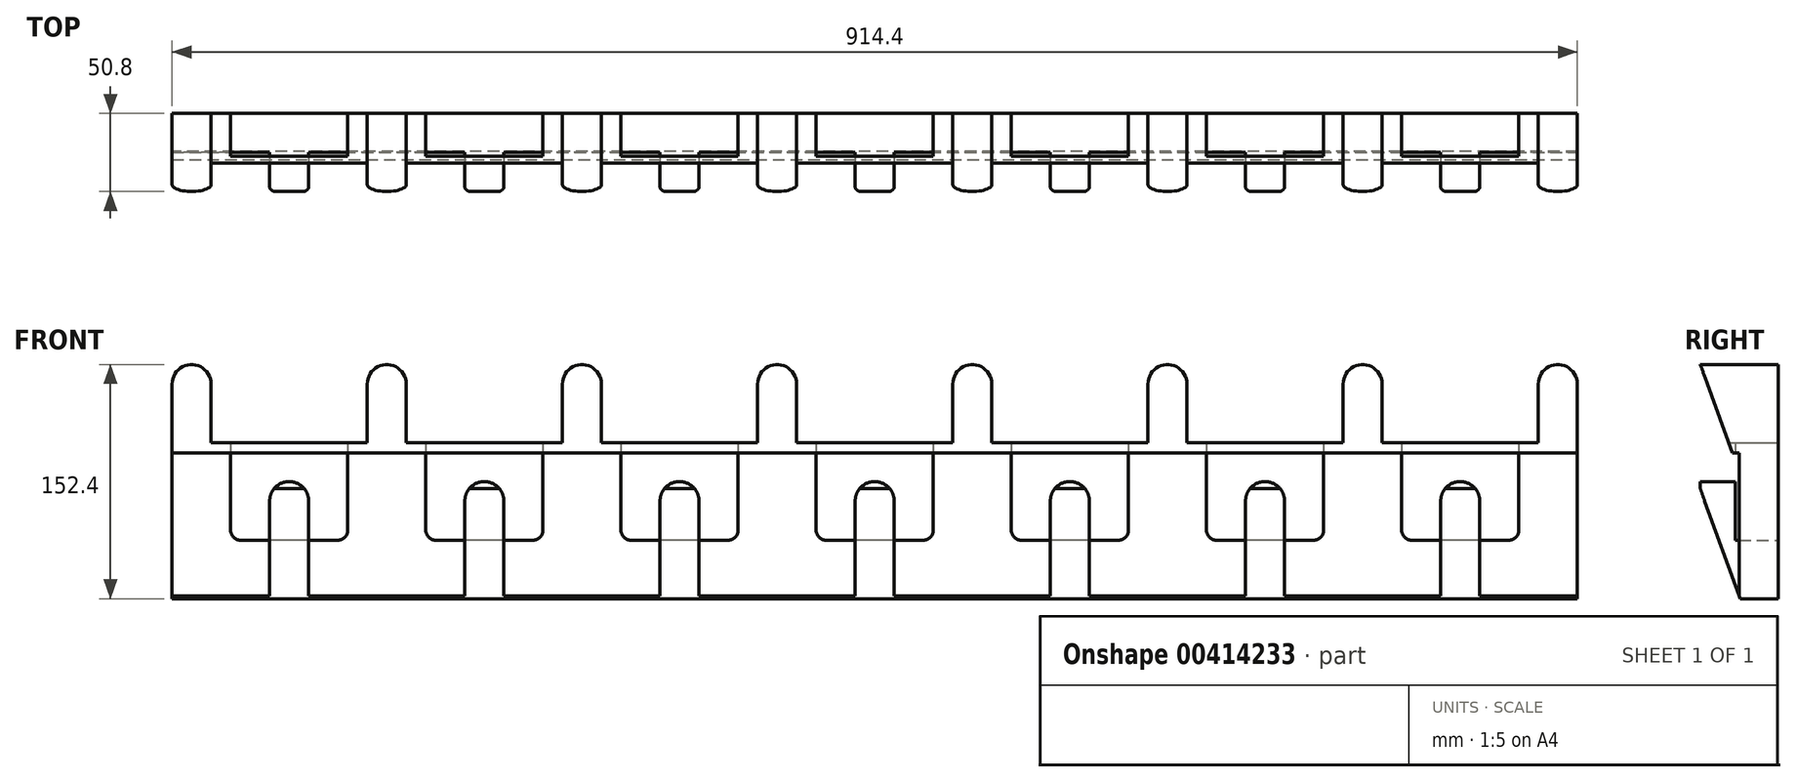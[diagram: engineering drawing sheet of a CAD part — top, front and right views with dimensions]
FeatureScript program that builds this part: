
annotation { "Feature Type Name" : "Feature", "Feature Type Description" : "" }
export const myFeature = defineFeature(function(context is Context, id is Id, definition is map)
    precondition{}
    {
        {
            var Q0;
            Q0=qCreatedBy(makeId("Right.planeOp"),FACE);
            var sketch = newSketch(context, id + "F0", { "sketchPlane" : qUnion([Q0])});
            skLineSegment(sketch, "E0.bottom", {"start": v(-50.8, 125.41) * mm, "end": v(0, 125.41) * mm});
            skLineSegment(sketch, "E0.top", {"start": v(-50.8, -26.99) * mm, "end": v(0, -26.99) * mm});
            skLineSegment(sketch, "E0.left", {"start": v(-50.8, 125.41) * mm, "end": v(-50.8, -26.99) * mm});
            skLineSegment(sketch, "E0.right", {"start": v(0, 125.41) * mm, "end": v(0, -26.99) * mm});
            skSolve(sketch);
        }
        {
            var Q0;
            Q0 = qSketchRegion(id + "F0", true);
            extrude(context, id + "F1", {"entities" : qUnion([Q0]), "depth" : 914.4 * mm});
        }
        {
            var Q0;
            Q0=makeQuery(id+"F1.opExtrude","SWEPT_FACE",FACE,{"disambiguationData":[OSD([sQuery(id+"F0.wireOp",EDGE,"E0.left")])]});
            var sketch = newSketch(context, id + "F2", { "sketchPlane" : qUnion([Q0])});
            skLineSegment(sketch, "E1.left", {"start": v(63.5, -26.99) * mm, "end": v(63.5, 36.51) * mm});
            skArc(sketch, "E2", {"start": v(88.9, 36.51) * mm, "mid": v(76.2, 49.21) * mm, "end": v(63.5, 36.51) * mm});
            skLineSegment(sketch, "E3", {"start": v(63.5, -26.99) * mm, "end": v(-24.16, -26.99) * mm});
            skLineSegment(sketch, "E4", {"start": v(88.9, 36.51) * mm, "end": v(88.9, -26.99) * mm});
            skArc(sketch, "E5.1.0.0", {"start": v(215.9, 36.51) * mm, "mid": v(203.2, 49.21) * mm, "end": v(190.5, 36.51) * mm});
            skLineSegment(sketch, "E5.1.0.1", {"start": v(215.9, 36.51) * mm, "end": v(215.9, -26.99) * mm});
            skLineSegment(sketch, "E5.1.0.2", {"start": v(190.5, -26.99) * mm, "end": v(190.5, 36.51) * mm});
            skArc(sketch, "E5.2.0.0", {"start": v(342.9, 36.51) * mm, "mid": v(330.2, 49.21) * mm, "end": v(317.5, 36.51) * mm});
            skLineSegment(sketch, "E5.2.0.1", {"start": v(342.9, 36.51) * mm, "end": v(342.9, -26.99) * mm});
            skLineSegment(sketch, "E5.2.0.2", {"start": v(317.5, -26.99) * mm, "end": v(317.5, 36.51) * mm});
            skArc(sketch, "E5.3.0.0", {"start": v(469.9, 36.51) * mm, "mid": v(457.2, 49.21) * mm, "end": v(444.5, 36.51) * mm});
            skLineSegment(sketch, "E5.3.0.1", {"start": v(469.9, 36.51) * mm, "end": v(469.9, -26.99) * mm});
            skLineSegment(sketch, "E5.3.0.2", {"start": v(444.5, -26.99) * mm, "end": v(444.5, 36.51) * mm});
            skArc(sketch, "E5.4.0.0", {"start": v(596.9, 36.51) * mm, "mid": v(584.2, 49.21) * mm, "end": v(571.5, 36.51) * mm});
            skLineSegment(sketch, "E5.4.0.1", {"start": v(596.9, 36.51) * mm, "end": v(596.9, -26.99) * mm});
            skLineSegment(sketch, "E5.4.0.2", {"start": v(571.5, -26.99) * mm, "end": v(571.5, 36.51) * mm});
            skArc(sketch, "E5.5.0.0", {"start": v(723.9, 36.51) * mm, "mid": v(711.2, 49.21) * mm, "end": v(698.5, 36.51) * mm});
            skLineSegment(sketch, "E5.5.0.1", {"start": v(723.9, 36.51) * mm, "end": v(723.9, -26.99) * mm});
            skLineSegment(sketch, "E5.5.0.2", {"start": v(698.5, -26.99) * mm, "end": v(698.5, 36.51) * mm});
            skArc(sketch, "E5.6.0.0", {"start": v(850.9, 36.51) * mm, "mid": v(838.2, 49.21) * mm, "end": v(825.5, 36.51) * mm});
            skLineSegment(sketch, "E5.6.0.1", {"start": v(850.9, 36.51) * mm, "end": v(850.9, -26.99) * mm});
            skLineSegment(sketch, "E5.6.0.2", {"start": v(825.5, -26.99) * mm, "end": v(825.5, 36.51) * mm});
            skLineSegment(sketch, "E5.direction1", {"start": v(63.5, -26.99) * mm, "end": v(190.5, -26.99) * mm, "construction": true});
            skLineSegment(sketch, "E6", {"start": v(88.9, -26.99) * mm, "end": v(190.5, -26.99) * mm});
            skLineSegment(sketch, "E7", {"start": v(215.9, -26.99) * mm, "end": v(317.5, -26.99) * mm});
            skLineSegment(sketch, "E8", {"start": v(342.9, -26.99) * mm, "end": v(444.5, -26.99) * mm});
            skLineSegment(sketch, "E9", {"start": v(469.9, -26.99) * mm, "end": v(571.5, -26.99) * mm});
            skLineSegment(sketch, "E10", {"start": v(596.9, -26.99) * mm, "end": v(698.5, -26.99) * mm});
            skLineSegment(sketch, "E11", {"start": v(723.9, -26.99) * mm, "end": v(825.5, -26.99) * mm});
            skLineSegment(sketch, "E12", {"start": v(850.9, -26.99) * mm, "end": v(949.6, -26.99) * mm});
            skLineSegment(sketch, "E13", {"start": v(949.6, -26.99) * mm, "end": v(949.6, 67.97) * mm});
            skLineSegment(sketch, "E14", {"start": v(949.6, 67.97) * mm, "end": v(-24.16, 67.97) * mm});
            skLineSegment(sketch, "E15", {"start": v(-24.16, 67.97) * mm, "end": v(-24.16, -26.99) * mm});
            skSolve(sketch);
        }
        {
            var Q0;
            Q0 = qSketchRegion(id + "F2", true);
            extrude(context, id + "F3", {"entities" : qUnion([Q0]), "operationType" : NewBodyOperationType.REMOVE, "oppositeDirection" : true, "depth" : 25.4 * mm});
        }
        {
            var Q0;
            Q0=qCreatedBy(makeId("Right.planeOp"),FACE);
            var sketch = newSketch(context, id + "F4", { "sketchPlane" : qUnion([Q0])});
            skLineSegment(sketch, "E16", {"start": v(-24.74, -26.99) * mm, "end": v(-50.8, 44.62) * mm});
            skLineSegment(sketch, "E17", {"start": v(-50.8, 44.62) * mm, "end": v(-50.8, -26.99) * mm});
            skLineSegment(sketch, "E18", {"start": v(-50.8, -26.99) * mm, "end": v(-24.74, -26.99) * mm});
            skSolve(sketch);
        }
        {
            var Q0;
            Q0 = qSketchRegion(id + "F4", true);
            extrude(context, id + "F5", {"entities" : qUnion([Q0]), "operationType" : NewBodyOperationType.REMOVE, "endBound" : BoundingType.THROUGH_ALL, "depth" : 25.4 * mm});
        }
        {
            var Q0;
            Q0=qCreatedBy(makeId("Right.planeOp"),FACE);
            var sketch = newSketch(context, id + "F6", { "sketchPlane" : qUnion([Q0])});
            skLineSegment(sketch, "E19", {"start": v(-29.08, 65.74) * mm, "end": v(-50.8, 125.41) * mm});
            skLineSegment(sketch, "E20", {"start": v(-50.8, 125.41) * mm, "end": v(-50.8, 65.74) * mm});
            skLineSegment(sketch, "E21", {"start": v(-50.8, 65.74) * mm, "end": v(-29.08, 65.74) * mm});
            skSolve(sketch);
        }
        {
            var Q0;
            Q0 = qSketchRegion(id + "F6", true);
            extrude(context, id + "F7", {"entities" : qUnion([Q0]), "operationType" : NewBodyOperationType.REMOVE, "endBound" : BoundingType.THROUGH_ALL, "depth" : 25.4 * mm});
        }
        {
            var Q0;
            Q0=qCreatedBy(makeId("Front.planeOp"),FACE);
            var sketch = newSketch(context, id + "F8", { "sketchPlane" : qUnion([Q0])});
            skLineSegment(sketch, "E22", {"start": v(0, 74.61) * mm, "end": v(0, 112.71) * mm});
            skLineSegment(sketch, "E23", {"start": v(25.4, 112.71) * mm, "end": v(25.4, 74.61) * mm});
            skArc(sketch, "E24", {"start": v(25.4, 112.71) * mm, "mid": v(12.7, 125.41) * mm, "end": v(0, 112.71) * mm});
            skLineSegment(sketch, "E25.1.0.0", {"start": v(152.4, 112.71) * mm, "end": v(152.4, 74.61) * mm});
            skArc(sketch, "E25.1.0.1", {"start": v(152.4, 112.71) * mm, "mid": v(139.7, 125.41) * mm, "end": v(127, 112.71) * mm});
            skLineSegment(sketch, "E25.1.0.2", {"start": v(127, 74.61) * mm, "end": v(127, 112.71) * mm});
            skLineSegment(sketch, "E25.2.0.0", {"start": v(279.4, 112.71) * mm, "end": v(279.4, 74.61) * mm});
            skArc(sketch, "E25.2.0.1", {"start": v(279.4, 112.71) * mm, "mid": v(266.7, 125.41) * mm, "end": v(254, 112.71) * mm});
            skLineSegment(sketch, "E25.2.0.2", {"start": v(254, 74.61) * mm, "end": v(254, 112.71) * mm});
            skLineSegment(sketch, "E25.3.0.0", {"start": v(406.4, 112.71) * mm, "end": v(406.4, 74.61) * mm});
            skArc(sketch, "E25.3.0.1", {"start": v(406.4, 112.71) * mm, "mid": v(393.7, 125.41) * mm, "end": v(381, 112.71) * mm});
            skLineSegment(sketch, "E25.3.0.2", {"start": v(381, 74.61) * mm, "end": v(381, 112.71) * mm});
            skLineSegment(sketch, "E25.4.0.0", {"start": v(533.4, 112.71) * mm, "end": v(533.4, 74.61) * mm});
            skArc(sketch, "E25.4.0.1", {"start": v(533.4, 112.71) * mm, "mid": v(520.7, 125.41) * mm, "end": v(508, 112.71) * mm});
            skLineSegment(sketch, "E25.4.0.2", {"start": v(508, 74.61) * mm, "end": v(508, 112.71) * mm});
            skLineSegment(sketch, "E25.5.0.0", {"start": v(660.4, 112.71) * mm, "end": v(660.4, 74.61) * mm});
            skArc(sketch, "E25.5.0.1", {"start": v(660.4, 112.71) * mm, "mid": v(647.7, 125.41) * mm, "end": v(635, 112.71) * mm});
            skLineSegment(sketch, "E25.5.0.2", {"start": v(635, 74.61) * mm, "end": v(635, 112.71) * mm});
            skLineSegment(sketch, "E25.6.0.0", {"start": v(787.4, 112.71) * mm, "end": v(787.4, 74.61) * mm});
            skArc(sketch, "E25.6.0.1", {"start": v(787.4, 112.71) * mm, "mid": v(774.7, 125.41) * mm, "end": v(762, 112.71) * mm});
            skLineSegment(sketch, "E25.6.0.2", {"start": v(762, 74.61) * mm, "end": v(762, 112.71) * mm});
            skLineSegment(sketch, "E25.direction1", {"start": v(0, 74.61) * mm, "end": v(127, 74.61) * mm, "construction": true});
            skLineSegment(sketch, "E26", {"start": v(25.4, 74.61) * mm, "end": v(127, 74.61) * mm});
            skLineSegment(sketch, "E27", {"start": v(152.4, 74.61) * mm, "end": v(254, 74.61) * mm});
            skLineSegment(sketch, "E28", {"start": v(279.4, 74.61) * mm, "end": v(381, 74.61) * mm});
            skLineSegment(sketch, "E29", {"start": v(508, 74.61) * mm, "end": v(406.4, 74.61) * mm});
            skLineSegment(sketch, "E30", {"start": v(533.4, 74.61) * mm, "end": v(635, 74.61) * mm});
            skLineSegment(sketch, "E31", {"start": v(660.4, 74.61) * mm, "end": v(762, 74.61) * mm});
            skLineSegment(sketch, "E32", {"start": v(957, 74.61) * mm, "end": v(957, 229.98) * mm});
            skLineSegment(sketch, "E33", {"start": v(957, 229.98) * mm, "end": v(-17.83, 229.98) * mm});
            skLineSegment(sketch, "E34", {"start": v(-17.83, 229.98) * mm, "end": v(-17.83, 74.61) * mm});
            skLineSegment(sketch, "E35", {"start": v(-17.83, 74.61) * mm, "end": v(0, 74.61) * mm});
            skLineSegment(sketch, "E36.0.7.0", {"start": v(914.4, 112.71) * mm, "end": v(914.4, 74.61) * mm});
            skArc(sketch, "E36.3.7.0", {"start": v(914.4, 112.71) * mm, "mid": v(901.7, 125.41) * mm, "end": v(889, 112.71) * mm});
            skLineSegment(sketch, "E36.7.7.0", {"start": v(889, 74.61) * mm, "end": v(889, 112.71) * mm});
            skLineSegment(sketch, "E37", {"start": v(914.4, 74.61) * mm, "end": v(957, 74.61) * mm});
            skLineSegment(sketch, "E38", {"start": v(787.4, 74.61) * mm, "end": v(889, 74.61) * mm});
            skSolve(sketch);
        }
        {
            var Q0;
            Q0 = qSketchRegion(id + "F8", true);
            extrude(context, id + "F9", {"entities" : qUnion([Q0]), "operationType" : NewBodyOperationType.REMOVE, "endBound" : BoundingType.THROUGH_ALL, "depth" : 25.4 * mm});
        }
        {
            var Q0;
            Q0=makeQuery(id+"F1.opExtrude","SWEPT_FACE",FACE,{"disambiguationData":[OSD([sQuery(id+"F0.wireOp",EDGE,"E0.right")])]});
            var sketch = newSketch(context, id + "F10", { "sketchPlane" : qUnion([Q0])});
            skLineSegment(sketch, "E39.bottom", {"start": v(-869.95, 112.71) * mm, "end": v(-806.45, 112.71) * mm});
            skLineSegment(sketch, "E39.top", {"start": v(-869.95, 11.11) * mm, "end": v(-806.45, 11.11) * mm});
            skLineSegment(sketch, "E39.left", {"start": v(-876.3, 106.36) * mm, "end": v(-876.3, 17.46) * mm});
            skLineSegment(sketch, "E39.right", {"start": v(-800.1, 106.36) * mm, "end": v(-800.1, 17.46) * mm});
            skPoint(sketch, "E40.visualSharp", {"position": v(-876.3, 112.71) * mm});
            skArc(sketch, "E40.filletArc", {"start": v(-869.95, 112.71) * mm, "mid": v(-874.44, 110.85) * mm, "end": v(-876.3, 106.36) * mm});
            skPoint(sketch, "E41.visualSharp", {"position": v(-800.1, 112.71) * mm});
            skArc(sketch, "E41.filletArc", {"start": v(-800.1, 106.36) * mm, "mid": v(-801.96, 110.85) * mm, "end": v(-806.45, 112.71) * mm});
            skPoint(sketch, "E42.visualSharp", {"position": v(-800.1, 11.11) * mm});
            skArc(sketch, "E42.filletArc", {"start": v(-806.45, 11.11) * mm, "mid": v(-801.96, 12.97) * mm, "end": v(-800.1, 17.46) * mm});
            skPoint(sketch, "E43.visualSharp", {"position": v(-876.3, 11.11) * mm});
            skArc(sketch, "E43.filletArc", {"start": v(-876.3, 17.46) * mm, "mid": v(-874.44, 12.97) * mm, "end": v(-869.95, 11.11) * mm});
            skLineSegment(sketch, "E44.1.0.0", {"start": v(-742.95, 112.71) * mm, "end": v(-679.45, 112.71) * mm});
            skLineSegment(sketch, "E44.1.0.1", {"start": v(-749.3, 106.36) * mm, "end": v(-749.3, 17.46) * mm});
            skPoint(sketch, "E44.1.0.2", {"position": v(-749.3, 112.71) * mm});
            skPoint(sketch, "E44.1.0.3", {"position": v(-673.1, 112.71) * mm});
            skLineSegment(sketch, "E44.1.0.4", {"start": v(-673.1, 106.36) * mm, "end": v(-673.1, 17.46) * mm});
            skPoint(sketch, "E44.1.0.5", {"position": v(-673.1, 11.11) * mm});
            skLineSegment(sketch, "E44.1.0.6", {"start": v(-742.95, 11.11) * mm, "end": v(-679.45, 11.11) * mm});
            skPoint(sketch, "E44.1.0.7", {"position": v(-749.3, 11.11) * mm});
            skArc(sketch, "E44.1.0.8", {"start": v(-742.95, 112.71) * mm, "mid": v(-747.44, 110.85) * mm, "end": v(-749.3, 106.36) * mm});
            skArc(sketch, "E44.1.0.9", {"start": v(-749.3, 17.46) * mm, "mid": v(-747.44, 12.97) * mm, "end": v(-742.95, 11.11) * mm});
            skArc(sketch, "E44.1.0.10", {"start": v(-673.1, 106.36) * mm, "mid": v(-674.96, 110.85) * mm, "end": v(-679.45, 112.71) * mm});
            skArc(sketch, "E44.1.0.11", {"start": v(-679.45, 11.11) * mm, "mid": v(-674.96, 12.97) * mm, "end": v(-673.1, 17.46) * mm});
            skLineSegment(sketch, "E44.2.0.0", {"start": v(-615.95, 112.71) * mm, "end": v(-552.45, 112.71) * mm});
            skLineSegment(sketch, "E44.2.0.1", {"start": v(-622.3, 106.36) * mm, "end": v(-622.3, 17.46) * mm});
            skPoint(sketch, "E44.2.0.2", {"position": v(-622.3, 112.71) * mm});
            skPoint(sketch, "E44.2.0.3", {"position": v(-546.1, 112.71) * mm});
            skLineSegment(sketch, "E44.2.0.4", {"start": v(-546.1, 106.36) * mm, "end": v(-546.1, 17.46) * mm});
            skPoint(sketch, "E44.2.0.5", {"position": v(-546.1, 11.11) * mm});
            skLineSegment(sketch, "E44.2.0.6", {"start": v(-615.95, 11.11) * mm, "end": v(-552.45, 11.11) * mm});
            skPoint(sketch, "E44.2.0.7", {"position": v(-622.3, 11.11) * mm});
            skArc(sketch, "E44.2.0.8", {"start": v(-615.95, 112.71) * mm, "mid": v(-620.44, 110.85) * mm, "end": v(-622.3, 106.36) * mm});
            skArc(sketch, "E44.2.0.9", {"start": v(-622.3, 17.46) * mm, "mid": v(-620.44, 12.97) * mm, "end": v(-615.95, 11.11) * mm});
            skArc(sketch, "E44.2.0.10", {"start": v(-546.1, 106.36) * mm, "mid": v(-547.96, 110.85) * mm, "end": v(-552.45, 112.71) * mm});
            skArc(sketch, "E44.2.0.11", {"start": v(-552.45, 11.11) * mm, "mid": v(-547.96, 12.97) * mm, "end": v(-546.1, 17.46) * mm});
            skLineSegment(sketch, "E44.3.0.0", {"start": v(-488.95, 112.71) * mm, "end": v(-425.45, 112.71) * mm});
            skLineSegment(sketch, "E44.3.0.1", {"start": v(-495.3, 106.36) * mm, "end": v(-495.3, 17.46) * mm});
            skPoint(sketch, "E44.3.0.2", {"position": v(-495.3, 112.71) * mm});
            skPoint(sketch, "E44.3.0.3", {"position": v(-419.1, 112.71) * mm});
            skLineSegment(sketch, "E44.3.0.4", {"start": v(-419.1, 106.36) * mm, "end": v(-419.1, 17.46) * mm});
            skPoint(sketch, "E44.3.0.5", {"position": v(-419.1, 11.11) * mm});
            skLineSegment(sketch, "E44.3.0.6", {"start": v(-488.95, 11.11) * mm, "end": v(-425.45, 11.11) * mm});
            skPoint(sketch, "E44.3.0.7", {"position": v(-495.3, 11.11) * mm});
            skArc(sketch, "E44.3.0.8", {"start": v(-488.95, 112.71) * mm, "mid": v(-493.44, 110.85) * mm, "end": v(-495.3, 106.36) * mm});
            skArc(sketch, "E44.3.0.9", {"start": v(-495.3, 17.46) * mm, "mid": v(-493.44, 12.97) * mm, "end": v(-488.95, 11.11) * mm});
            skArc(sketch, "E44.3.0.10", {"start": v(-419.1, 106.36) * mm, "mid": v(-420.96, 110.85) * mm, "end": v(-425.45, 112.71) * mm});
            skArc(sketch, "E44.3.0.11", {"start": v(-425.45, 11.11) * mm, "mid": v(-420.96, 12.97) * mm, "end": v(-419.1, 17.46) * mm});
            skLineSegment(sketch, "E44.4.0.0", {"start": v(-361.95, 112.71) * mm, "end": v(-298.45, 112.71) * mm});
            skLineSegment(sketch, "E44.4.0.1", {"start": v(-368.3, 106.36) * mm, "end": v(-368.3, 17.46) * mm});
            skPoint(sketch, "E44.4.0.2", {"position": v(-368.3, 112.71) * mm});
            skPoint(sketch, "E44.4.0.3", {"position": v(-292.1, 112.71) * mm});
            skLineSegment(sketch, "E44.4.0.4", {"start": v(-292.1, 106.36) * mm, "end": v(-292.1, 17.46) * mm});
            skPoint(sketch, "E44.4.0.5", {"position": v(-292.1, 11.11) * mm});
            skLineSegment(sketch, "E44.4.0.6", {"start": v(-361.95, 11.11) * mm, "end": v(-298.45, 11.11) * mm});
            skPoint(sketch, "E44.4.0.7", {"position": v(-368.3, 11.11) * mm});
            skArc(sketch, "E44.4.0.8", {"start": v(-361.95, 112.71) * mm, "mid": v(-366.44, 110.85) * mm, "end": v(-368.3, 106.36) * mm});
            skArc(sketch, "E44.4.0.9", {"start": v(-368.3, 17.46) * mm, "mid": v(-366.44, 12.97) * mm, "end": v(-361.95, 11.11) * mm});
            skArc(sketch, "E44.4.0.10", {"start": v(-292.1, 106.36) * mm, "mid": v(-293.96, 110.85) * mm, "end": v(-298.45, 112.71) * mm});
            skArc(sketch, "E44.4.0.11", {"start": v(-298.45, 11.11) * mm, "mid": v(-293.96, 12.97) * mm, "end": v(-292.1, 17.46) * mm});
            skLineSegment(sketch, "E44.5.0.0", {"start": v(-234.95, 112.71) * mm, "end": v(-171.45, 112.71) * mm});
            skLineSegment(sketch, "E44.5.0.1", {"start": v(-241.3, 106.36) * mm, "end": v(-241.3, 17.46) * mm});
            skPoint(sketch, "E44.5.0.2", {"position": v(-241.3, 112.71) * mm});
            skPoint(sketch, "E44.5.0.3", {"position": v(-165.1, 112.71) * mm});
            skLineSegment(sketch, "E44.5.0.4", {"start": v(-165.1, 106.36) * mm, "end": v(-165.1, 17.46) * mm});
            skPoint(sketch, "E44.5.0.5", {"position": v(-165.1, 11.11) * mm});
            skLineSegment(sketch, "E44.5.0.6", {"start": v(-234.95, 11.11) * mm, "end": v(-171.45, 11.11) * mm});
            skPoint(sketch, "E44.5.0.7", {"position": v(-241.3, 11.11) * mm});
            skArc(sketch, "E44.5.0.8", {"start": v(-234.95, 112.71) * mm, "mid": v(-239.44, 110.85) * mm, "end": v(-241.3, 106.36) * mm});
            skArc(sketch, "E44.5.0.9", {"start": v(-241.3, 17.46) * mm, "mid": v(-239.44, 12.97) * mm, "end": v(-234.95, 11.11) * mm});
            skArc(sketch, "E44.5.0.10", {"start": v(-165.1, 106.36) * mm, "mid": v(-166.96, 110.85) * mm, "end": v(-171.45, 112.71) * mm});
            skArc(sketch, "E44.5.0.11", {"start": v(-171.45, 11.11) * mm, "mid": v(-166.96, 12.97) * mm, "end": v(-165.1, 17.46) * mm});
            skLineSegment(sketch, "E44.6.0.0", {"start": v(-107.95, 112.71) * mm, "end": v(-44.45, 112.71) * mm});
            skLineSegment(sketch, "E44.6.0.1", {"start": v(-114.3, 106.36) * mm, "end": v(-114.3, 17.46) * mm});
            skPoint(sketch, "E44.6.0.2", {"position": v(-114.3, 112.71) * mm});
            skPoint(sketch, "E44.6.0.3", {"position": v(-38.1, 112.71) * mm});
            skLineSegment(sketch, "E44.6.0.4", {"start": v(-38.1, 106.36) * mm, "end": v(-38.1, 17.46) * mm});
            skPoint(sketch, "E44.6.0.5", {"position": v(-38.1, 11.11) * mm});
            skLineSegment(sketch, "E44.6.0.6", {"start": v(-107.95, 11.11) * mm, "end": v(-44.45, 11.11) * mm});
            skPoint(sketch, "E44.6.0.7", {"position": v(-114.3, 11.11) * mm});
            skArc(sketch, "E44.6.0.8", {"start": v(-107.95, 112.71) * mm, "mid": v(-112.44, 110.85) * mm, "end": v(-114.3, 106.36) * mm});
            skArc(sketch, "E44.6.0.9", {"start": v(-114.3, 17.46) * mm, "mid": v(-112.44, 12.97) * mm, "end": v(-107.95, 11.11) * mm});
            skArc(sketch, "E44.6.0.10", {"start": v(-38.1, 106.36) * mm, "mid": v(-39.96, 110.85) * mm, "end": v(-44.45, 112.71) * mm});
            skArc(sketch, "E44.6.0.11", {"start": v(-44.45, 11.11) * mm, "mid": v(-39.96, 12.97) * mm, "end": v(-38.1, 17.46) * mm});
            skLineSegment(sketch, "E44.direction1", {"start": v(-876.3, 11.11) * mm, "end": v(-749.3, 11.11) * mm, "construction": true});
            skSolve(sketch);
        }
        {
            var Q0;
            Q0 = qSketchRegion(id + "F10", true);
            extrude(context, id + "F11", {"entities" : qUnion([Q0]), "operationType" : NewBodyOperationType.REMOVE, "oppositeDirection" : true, "depth" : 27.94 * mm});
        }
    });
